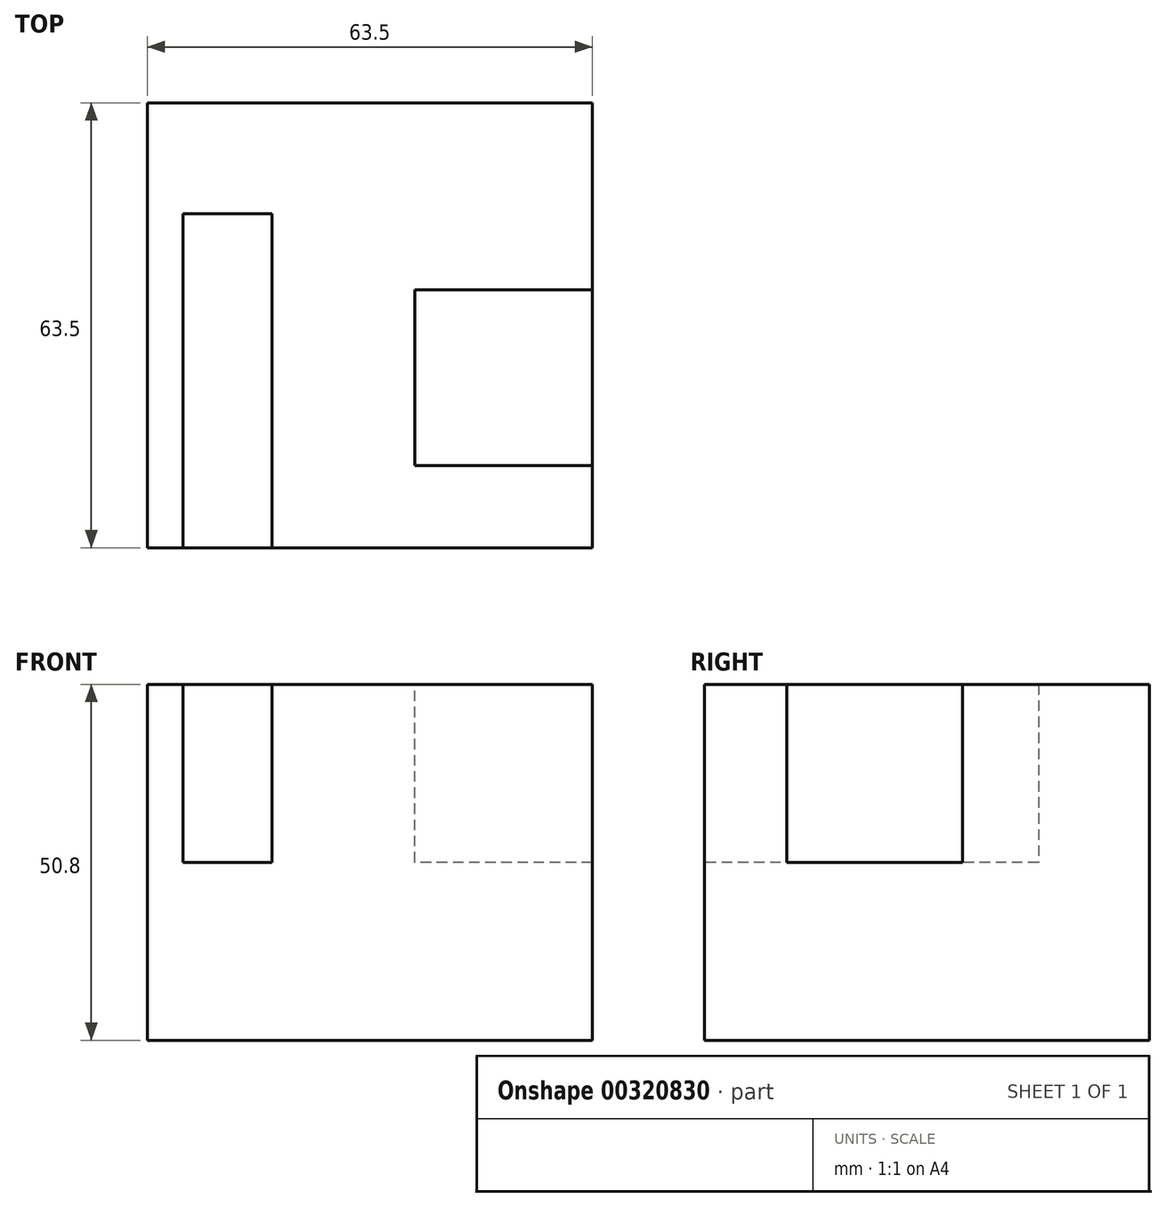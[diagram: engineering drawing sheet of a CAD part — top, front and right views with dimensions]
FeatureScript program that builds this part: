
annotation { "Feature Type Name" : "Feature", "Feature Type Description" : "" }
export const myFeature = defineFeature(function(context is Context, id is Id, definition is map)
    precondition{}
    {
        {
            var Q0;
            Q0=qCreatedBy(makeId("Front.planeOp"),FACE);
            var sketch = newSketch(context, id + "F0", { "sketchPlane" : qUnion([Q0])});
            skLineSegment(sketch, "E0.bottom", {"start": v(-21.34, 20.21) * mm, "end": v(42.16, 20.21) * mm});
            skLineSegment(sketch, "E0.top", {"start": v(-21.34, -30.59) * mm, "end": v(42.16, -30.59) * mm});
            skLineSegment(sketch, "E0.left", {"start": v(-21.34, 20.21) * mm, "end": v(-21.34, -30.59) * mm});
            skLineSegment(sketch, "E0.right", {"start": v(42.16, 20.21) * mm, "end": v(42.16, -30.59) * mm});
            skSolve(sketch);
        }
        {
            var Q0;
            Q0=makeQuery(id+"F0.imprint","IMPRINT",FACE,{"disambiguationData":[TD([[makeQuery(id+"F0.imprint","IMPRINT",EDGE,{"derivedFrom":sQuery(id+"F0.wireOp",EDGE,"E0.bottom")}),-1.0]])]});
            extrude(context, id + "F1", {"entities" : qUnion([Q0]), "depth" : 63.5 * mm});
        }
        {
            var Q0;
            Q0=makeQuery(id+"F1.opExtrude","SWEPT_FACE",FACE,{"disambiguationData":[OSD([sQuery(id+"F0.wireOp",EDGE,"E0.bottom")])]});
            var sketch = newSketch(context, id + "F2", { "sketchPlane" : qUnion([Q0])});
            skLineSegment(sketch, "E1.bottom", {"start": v(-3.56, 0) * mm, "end": v(-16.26, 0) * mm});
            skLineSegment(sketch, "E1.top", {"start": v(-3.56, -63.5) * mm, "end": v(-16.26, -63.5) * mm});
            skLineSegment(sketch, "E1.left", {"start": v(-3.56, 0) * mm, "end": v(-3.56, -63.5) * mm});
            skLineSegment(sketch, "E1.right", {"start": v(-16.26, 0) * mm, "end": v(-16.26, -63.5) * mm});
            skLineSegment(sketch, "E2.bottom", {"start": v(42.16, -26.67) * mm, "end": v(16.83, -26.67) * mm});
            skLineSegment(sketch, "E2.top", {"start": v(42.16, -51.77) * mm, "end": v(16.83, -51.77) * mm});
            skLineSegment(sketch, "E2.left", {"start": v(42.16, -26.67) * mm, "end": v(42.16, -51.77) * mm});
            skLineSegment(sketch, "E2.right", {"start": v(16.83, -26.67) * mm, "end": v(16.83, -51.77) * mm});
            skSolve(sketch);
        }
        {
            var Q0;
            Q0=makeQuery(id+"F2.imprint","IMPRINT",FACE,{"disambiguationData":[TD([[makeQuery(id+"F2.imprint","IMPRINT",EDGE,{"derivedFrom":sQuery(id+"F2.wireOp",EDGE,"E2.bottom")}),1.0]])]});
            var Q1;
            Q1=makeQuery(id+"F2.imprint","IMPRINT",FACE,{"disambiguationData":[TD([[makeQuery(id+"F2.imprint","IMPRINT",EDGE,{"derivedFrom":sQuery(id+"F2.wireOp",EDGE,"E1.bottom")}),-1.0]])]});
            extrude(context, id + "F3", {"entities" : qUnion([Q0, Q1]), "operationType" : NewBodyOperationType.REMOVE, "oppositeDirection" : true, "depth" : 25.4 * mm});
        }
        {
            var Q0;
            Q0=makeQuery(id+"F3.boolean.opBoolean","COPY",FACE,{"derivedFrom":makeQuery(id+"F3.opExtrude","CAP_FACE",FACE,{"disambiguationData":[OSD([sQuery(id+"F2.wireOp",EDGE,"E1.bottom"),sQuery(id+"F2.wireOp",EDGE,"E1.top"),sQuery(id+"F2.wireOp",EDGE,"E1.left"),sQuery(id+"F2.wireOp",EDGE,"E1.right")])],"isStart":false})});
            var sketch = newSketch(context, id + "F4", { "sketchPlane" : qUnion([Q0])});
            skLineSegment(sketch, "E3.bottom", {"start": v(-16.26, 0) * mm, "end": v(-3.56, 0) * mm});
            skLineSegment(sketch, "E3.top", {"start": v(-16.26, -15.83) * mm, "end": v(-3.56, -15.83) * mm});
            skLineSegment(sketch, "E3.left", {"start": v(-16.26, 0) * mm, "end": v(-16.26, -15.83) * mm});
            skLineSegment(sketch, "E3.right", {"start": v(-3.56, 0) * mm, "end": v(-3.56, -15.83) * mm});
            skSolve(sketch);
        }
        {
            var Q0;
            Q0=makeQuery(id+"F4.imprint","IMPRINT",FACE,{"disambiguationData":[TD([[makeQuery(id+"F4.imprint","IMPRINT",EDGE,{"derivedFrom":sQuery(id+"F4.wireOp",EDGE,"E3.bottom")}),-1.0]])]});
            extrude(context, id + "F5", {"entities" : qUnion([Q0]), "operationType" : NewBodyOperationType.ADD, "depth" : 25.4 * mm});
        }
    });
